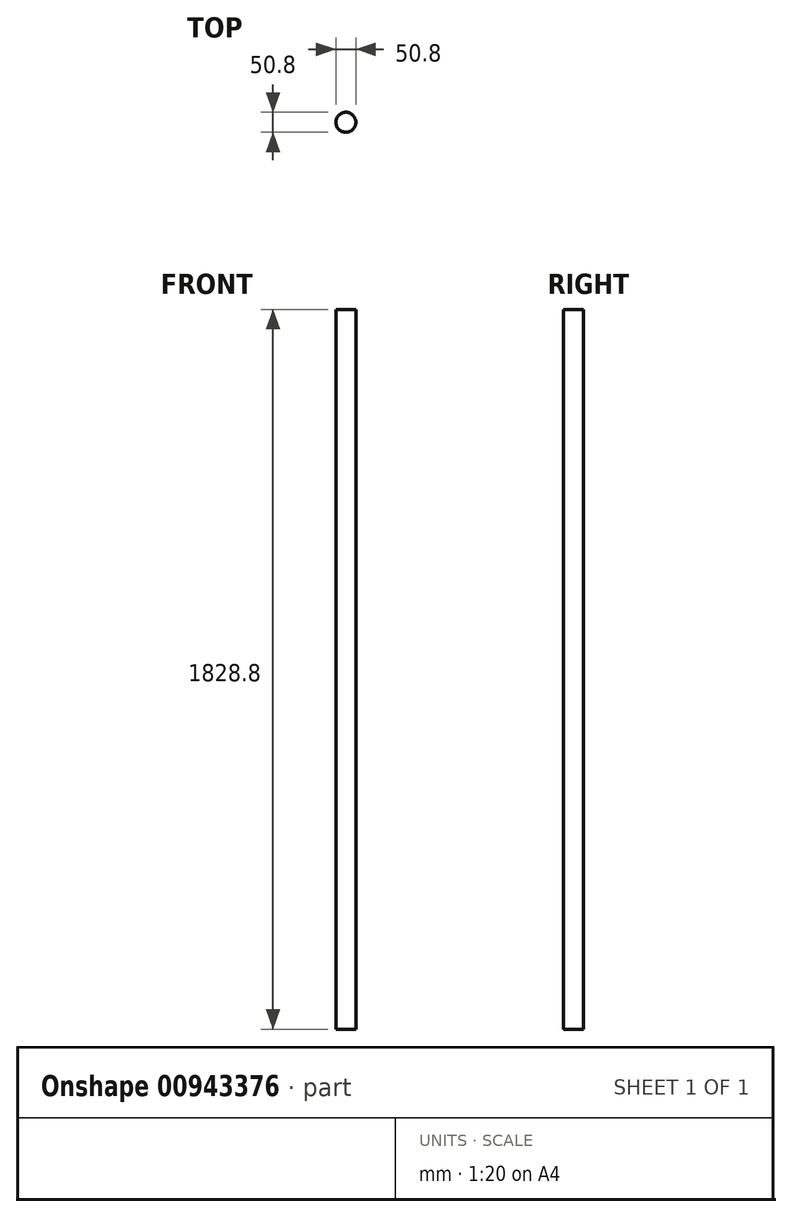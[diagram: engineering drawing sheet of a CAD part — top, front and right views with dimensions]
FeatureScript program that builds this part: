
annotation { "Feature Type Name" : "Feature", "Feature Type Description" : "" }
export const myFeature = defineFeature(function(context is Context, id is Id, definition is map)
    precondition{}
    {
        {
            var Q0;
            Q0=qCreatedBy(makeId("Top.planeOp"),FACE);
            var sketch = newSketch(context, id + "F0", { "sketchPlane" : qUnion([Q0])});
            skCircle(sketch, "E0", {"center": v(0, 0) * mm, "radius": 25.4 * mm});
            skSolve(sketch);
        }
        {
            var Q0;
            Q0=makeQuery(id+"F0.imprint","IMPRINT",FACE,{"disambiguationData":[TD([[makeQuery(id+"F0.imprint","IMPRINT",EDGE,{"derivedFrom":sQuery(id+"F0.wireOp",EDGE,"E0")}),1.0]])]});
            extrude(context, id + "F1", {"entities" : qUnion([Q0]), "depth" : 1828.8 * mm, "offsetDistance" : 25.4 * mm});
        }
    });
